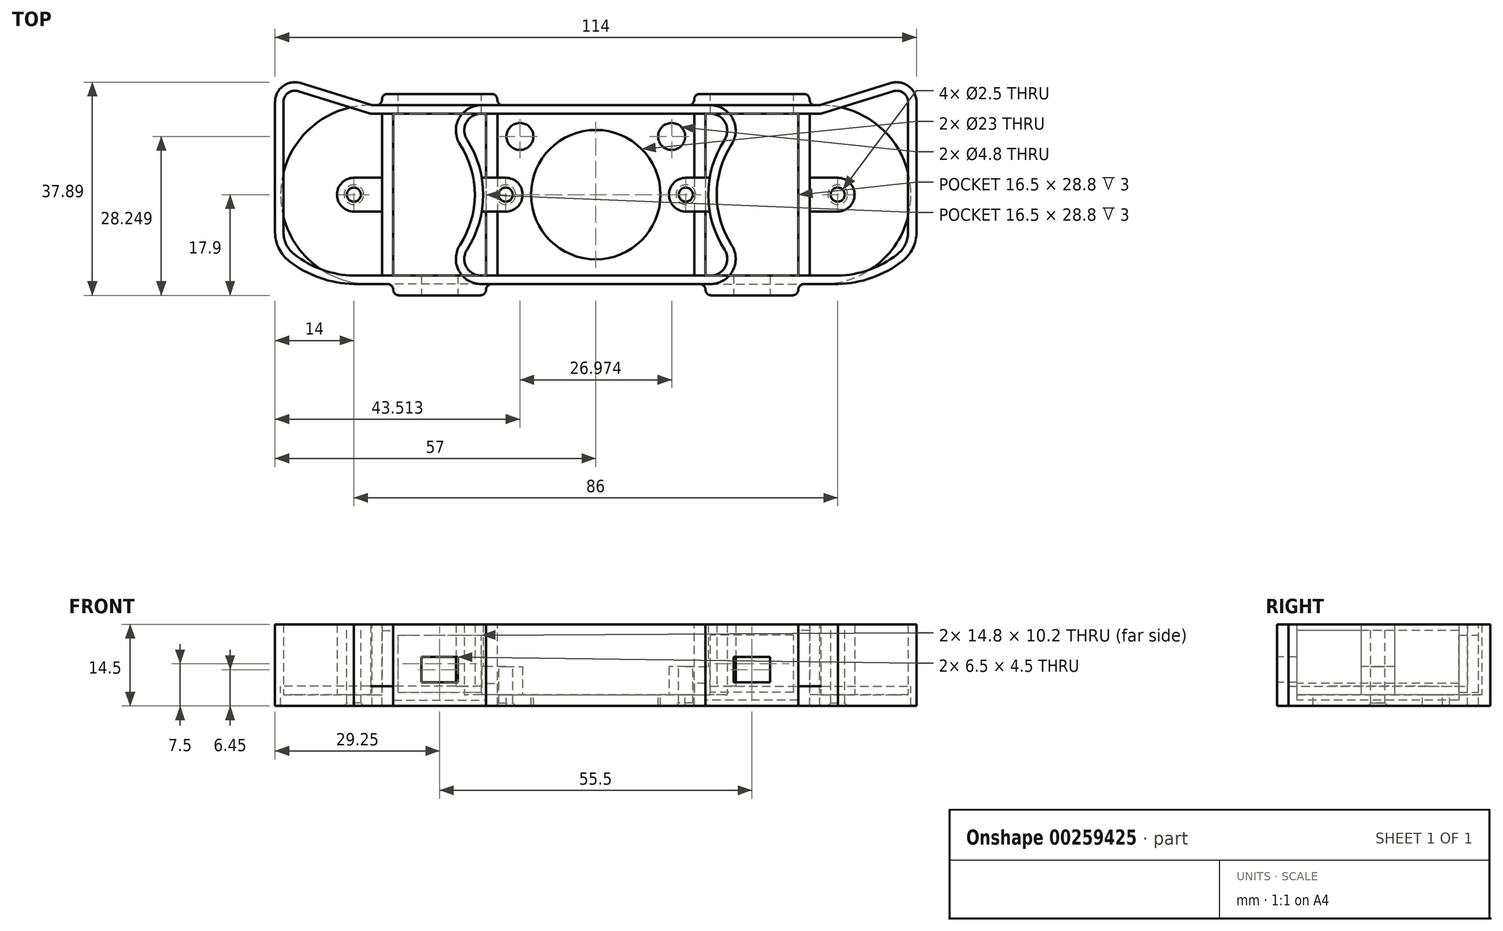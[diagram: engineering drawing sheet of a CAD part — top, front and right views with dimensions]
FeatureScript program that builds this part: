
annotation { "Feature Type Name" : "Feature", "Feature Type Description" : "" }
export const myFeature = defineFeature(function(context is Context, id is Id, definition is map)
    precondition{}
    {
        {
            var Q0;
            Q0=qCreatedBy(makeId("Top.planeOp"),FACE);
            var sketch = newSketch(context, id + "F0", { "sketchPlane" : qUnion([Q0])});
            skCircle(sketch, "E0", {"center": v(16, 0) * mm, "radius": 1.25 * mm});
            skCircle(sketch, "E1", {"center": v(-43, 0) * mm, "radius": 1.25 * mm});
            skCircle(sketch, "E2", {"center": v(0, 0) * mm, "radius": 11.5 * mm});
            skLineSegment(sketch, "E3", {"start": v(-40, 14.4) * mm, "end": v(20, 14.4) * mm});
            skLineSegment(sketch, "E4", {"start": v(-43, -14.4) * mm, "end": v(20, -14.4) * mm});
            skCircle(sketch, "E5", {"center": v(13.49, 10.35) * mm, "radius": 2.4 * mm});
            skLineSegment(sketch, "E6", {"start": v(-55.5, 14.4) * mm, "end": v(-55.5, -6.69) * mm});
            skLineSegment(sketch, "E7", {"start": v(20, 14.4) * mm, "end": v(20, -14.4) * mm, "construction": true});
            skArc(sketch, "E8", {"start": v(22.88, 9.77) * mm, "mid": v(20, 0) * mm, "end": v(22.88, -9.77) * mm});
            skLineSegment(sketch, "E9", {"start": v(20, 14.4) * mm, "end": v(20.36, 14.4) * mm});
            skLineSegment(sketch, "E10", {"start": v(20, -14.4) * mm, "end": v(20.36, -14.4) * mm});
            skPoint(sketch, "E11.visualSharp", {"position": v(27.2, 14.4) * mm});
            skArc(sketch, "E11.filletArc", {"start": v(22.88, 9.77) * mm, "mid": v(23, 12.83) * mm, "end": v(20.36, 14.4) * mm});
            skPoint(sketch, "E12.visualSharp", {"position": v(27.2, -14.4) * mm});
            skArc(sketch, "E12.filletArc", {"start": v(20.36, -14.4) * mm, "mid": v(23, -12.83) * mm, "end": v(22.88, -9.77) * mm});
            skLineSegment(sketch, "E13", {"start": v(-40, 14.4) * mm, "end": v(-52.9, 18.4) * mm});
            skLineSegment(sketch, "E14", {"start": v(-55.5, 16.49) * mm, "end": v(-55.5, 14.4) * mm});
            skLineSegment(sketch, "E15", {"start": v(-55.5, 14.4) * mm, "end": v(-40, 14.4) * mm, "construction": true});
            skArc(sketch, "E16", {"start": v(-53.56, -10.64) * mm, "mid": v(-48.58, -13.36) * mm, "end": v(-43, -14.4) * mm});
            skPoint(sketch, "E17.orphan", {"position": v(-55.5, -14.4) * mm});
            skPoint(sketch, "E18.visualSharp", {"position": v(-55.5, 19.2) * mm});
            skArc(sketch, "E18.filletArc", {"start": v(-52.9, 18.4) * mm, "mid": v(-54.69, 18.1) * mm, "end": v(-55.5, 16.49) * mm});
            skPoint(sketch, "E19.visualSharp", {"position": v(-55.5, -8.9) * mm});
            skArc(sketch, "E19.filletArc", {"start": v(-55.5, -6.69) * mm, "mid": v(-54.99, -8.89) * mm, "end": v(-53.56, -10.64) * mm});
            skLineSegment(sketch, "E20.0", {"start": v(-39.77, 15.9) * mm, "end": v(-52.46, 19.83) * mm});
            skArc(sketch, "E20.1", {"start": v(-52.46, 19.83) * mm, "mid": v(-55.58, 19.3) * mm, "end": v(-57, 16.49) * mm});
            skArc(sketch, "E20.2", {"start": v(20.36, -15.9) * mm, "mid": v(24.32, -13.55) * mm, "end": v(24.14, -8.96) * mm});
            skArc(sketch, "E20.3", {"start": v(24.14, 8.96) * mm, "mid": v(21.5, 0) * mm, "end": v(24.14, -8.96) * mm});
            skArc(sketch, "E20.4", {"start": v(24.14, 8.96) * mm, "mid": v(24.32, 13.55) * mm, "end": v(20.36, 15.9) * mm});
            skLineSegment(sketch, "E20.5", {"start": v(20, 15.9) * mm, "end": v(20.36, 15.9) * mm});
            skLineSegment(sketch, "E20.6", {"start": v(20, -15.9) * mm, "end": v(20.36, -15.9) * mm});
            skLineSegment(sketch, "E20.7", {"start": v(-43.02, -15.9) * mm, "end": v(20, -15.9) * mm});
            skLineSegment(sketch, "E20.8", {"start": v(-39.77, 15.9) * mm, "end": v(20, 15.9) * mm});
            skArc(sketch, "E20.9", {"start": v(-54.48, -11.83) * mm, "mid": v(-49.07, -14.78) * mm, "end": v(-43.02, -15.9) * mm});
            skArc(sketch, "E20.10", {"start": v(-57, -6.69) * mm, "mid": v(-56.34, -9.55) * mm, "end": v(-54.48, -11.83) * mm});
            skLineSegment(sketch, "E20.11", {"start": v(-57, 14.4) * mm, "end": v(-57, -6.69) * mm});
            skLineSegment(sketch, "E20.12", {"start": v(-57, 16.49) * mm, "end": v(-57, 14.4) * mm});
            skCircle(sketch, "E21", {"center": v(40.1, 0) * mm, "radius": 15.9 * mm});
            skLineSegment(sketch, "E22", {"start": v(20.36, 15.9) * mm, "end": v(40.1, 15.9) * mm});
            skLineSegment(sketch, "E23", {"start": v(20.36, -15.9) * mm, "end": v(40.1, -15.9) * mm});
            skLineSegment(sketch, "E24", {"start": v(-36, 14.4) * mm, "end": v(-36, -14.4) * mm});
            skLineSegment(sketch, "E25", {"start": v(-19.5, 14.4) * mm, "end": v(-19.5, -14.4) * mm});
            skLineSegment(sketch, "E26", {"start": v(-17.5, 14.4) * mm, "end": v(-17.5, -14.4) * mm});
            skLineSegment(sketch, "E27", {"start": v(-38, 14.4) * mm, "end": v(-38, -14.4) * mm});
            skArc(sketch, "E28", {"start": v(-43, 3) * mm, "mid": v(-46, 0) * mm, "end": v(-43, -3) * mm});
            skLineSegment(sketch, "E29", {"start": v(-43, -3) * mm, "end": v(-38, -3) * mm});
            skLineSegment(sketch, "E30", {"start": v(-43, 3) * mm, "end": v(-38, 3) * mm});
            skArc(sketch, "E31", {"start": v(16, 3) * mm, "mid": v(13, 0) * mm, "end": v(16, -3) * mm});
            skLineSegment(sketch, "E32", {"start": v(16, 3) * mm, "end": v(20.25, 3) * mm});
            skLineSegment(sketch, "E33", {"start": v(16, -3) * mm, "end": v(20.25, -3) * mm});
            skLineSegment(sketch, "E34", {"start": v(-38, 15.9) * mm, "end": v(-38, 17.9) * mm});
            skLineSegment(sketch, "E35", {"start": v(-38, 17.9) * mm, "end": v(-17.5, 17.9) * mm});
            skLineSegment(sketch, "E36", {"start": v(-17.5, 17.9) * mm, "end": v(-17.5, 15.9) * mm});
            skLineSegment(sketch, "E37", {"start": v(-36, -15.9) * mm, "end": v(-36, -17.9) * mm});
            skLineSegment(sketch, "E38", {"start": v(-36, -17.9) * mm, "end": v(-19.5, -17.9) * mm});
            skLineSegment(sketch, "E39", {"start": v(-19.5, -17.9) * mm, "end": v(-19.5, -15.9) * mm});
            skLineSegment(sketch, "E40", {"start": v(-35, 17.9) * mm, "end": v(-35, 14.4) * mm});
            skLineSegment(sketch, "E41", {"start": v(-20.5, 17.9) * mm, "end": v(-20.5, 14.4) * mm});
            skLineSegment(sketch, "E42", {"start": v(-31, -14.4) * mm, "end": v(-31, -17.9) * mm});
            skLineSegment(sketch, "E43", {"start": v(-24.5, -14.4) * mm, "end": v(-24.5, -17.9) * mm});
            skSolve(sketch);
        }
        {
            var Q0;
            Q0 = qSketchRegion(id + "F0", true);
            var Q1;
            Q1=makeQuery(id+"F0.imprint","IMPRINT",FACE,{"disambiguationData":[TD([[makeQuery(id+"F0.imprint","IMPRINT",EDGE,{"derivedFrom":sQuery(id+"F0.wireOp",EDGE,"E2")}),-1.0]])]});
            var Q2;
            {var subQ0=sQuery(id+"F0.wireOp",EDGE,"E40");var subQ1=sQuery(id+"F0.wireOp",EDGE,"E3");var subQ2=makeQuery(id+"F0.imprint","INTERSECT",VERTEX,{"derivedFrom":[subQ1,subQ0]});Q2=makeQuery(id+"F0.imprint","IMPRINT",FACE,{"disambiguationData":[TD([[makeQuery(id+"F0.imprint","IMPRINT",EDGE,{"disambiguationData":[TD([[subQ2,-1.0]])],"derivedFrom":subQ1}),1.0]])]});}
            var Q3;
            {var subQ0=sQuery(id+"F0.wireOp",EDGE,"E24");Q3=makeQuery(id+"F0.imprint","IMPRINT",FACE,{"disambiguationData":[TD([[makeQuery(id+"F0.imprint","IMPRINT",EDGE,{"derivedFrom":subQ0}),1.0]])]});}
            var Q4;
            {var subQ4=sQuery(id+"F0.wireOp",EDGE,"E24");Q4=makeQuery(id+"F0.imprint","IMPRINT",FACE,{"disambiguationData":[TD([[makeQuery(id+"F0.imprint","IMPRINT",EDGE,{"derivedFrom":subQ4}),-1.0]])]});}
            var Q5;
            Q5=makeQuery(id+"F0.imprint","IMPRINT",FACE,{"disambiguationData":[TD([[makeQuery(id+"F0.imprint","IMPRINT",EDGE,{"derivedFrom":sQuery(id+"F0.wireOp",EDGE,"E1")}),-1.0]])]});
            var Q6;
            Q6=makeQuery(id+"F0.imprint","IMPRINT",FACE,{"disambiguationData":[TD([[makeQuery(id+"F0.imprint","IMPRINT",EDGE,{"derivedFrom":sQuery(id+"F0.wireOp",EDGE,"E6")}),1.0]])]});
            var Q7;
            {var subQ0=sQuery(id+"F0.wireOp",EDGE,"E25");Q7=makeQuery(id+"F0.imprint","IMPRINT",FACE,{"disambiguationData":[TD([[makeQuery(id+"F0.imprint","IMPRINT",EDGE,{"derivedFrom":subQ0}),1.0]])]});}
            var Q8;
            Q8=makeQuery(id+"F0.imprint","IMPRINT",FACE,{"disambiguationData":[TD([[makeQuery(id+"F0.imprint","IMPRINT",EDGE,{"derivedFrom":sQuery(id+"F0.wireOp",EDGE,"E0")}),-1.0]])]});
            var Q9;
            {var subQ0=sQuery(id+"F0.wireOp",EDGE,"E42");var subQ1=sQuery(id+"F0.wireOp",EDGE,"E4");var subQ2=makeQuery(id+"F0.imprint","INTERSECT",VERTEX,{"derivedFrom":[subQ1,subQ0]});Q9=makeQuery(id+"F0.imprint","IMPRINT",FACE,{"disambiguationData":[TD([[makeQuery(id+"F0.imprint","IMPRINT",EDGE,{"disambiguationData":[TD([[subQ2,-1.0]])],"derivedFrom":subQ1}),-1.0]])]});}
            extrude(context, id + "F1", {"entities" : qUnion([Q0, Q1, Q2, Q3, Q4, Q5, Q6, Q7, Q8, Q9]), "oppositeDirection" : true, "depth" : 2 * mm});
        }
        {
            var Q0;
            Q0=makeQuery(id+"F0.imprint","IMPRINT",FACE,{"disambiguationData":[TD([[makeQuery(id+"F0.imprint","IMPRINT",EDGE,{"derivedFrom":sQuery(id+"F0.wireOp",EDGE,"E20.2")}),-1.0]])]});
            var Q1;
            {var subQ0=sQuery(id+"F0.wireOp",EDGE,"E21");var subQ1=makeQuery(id+"F0.imprint","INTERSECT",VERTEX,{"derivedFrom":[subQ0,sQuery(id+"F0.wireOp",EDGE,"E22")]});Q1=makeQuery(id+"F0.imprint","IMPRINT",FACE,{"disambiguationData":[TD([[makeQuery(id+"F0.imprint","IMPRINT",EDGE,{"disambiguationData":[TD([[subQ1,-1.0]])],"derivedFrom":subQ0}),1.0]])]});}
            extrude(context, id + "F2", {"entities" : qUnion([Q0, Q1]), "operationType" : NewBodyOperationType.ADD, "depth" : 1.5 * mm});
        }
        {
            var Q0;
            {var subQ4=sQuery(id+"F0.wireOp",EDGE,"E24");Q0=makeQuery(id+"F0.imprint","IMPRINT",FACE,{"disambiguationData":[TD([[makeQuery(id+"F0.imprint","IMPRINT",EDGE,{"derivedFrom":subQ4}),-1.0]])]});}
            extrude(context, id + "F3", {"entities" : qUnion([Q0]), "operationType" : NewBodyOperationType.ADD, "depth" : 11.4 * mm});
        }
        {
            var Q0;
            {var subQ0=sQuery(id+"F0.wireOp",EDGE,"E25");Q0=makeQuery(id+"F0.imprint","IMPRINT",FACE,{"disambiguationData":[TD([[makeQuery(id+"F0.imprint","IMPRINT",EDGE,{"derivedFrom":subQ0}),1.0]])]});}
            extrude(context, id + "F4", {"entities" : qUnion([Q0]), "operationType" : NewBodyOperationType.ADD, "depth" : 2 * mm});
        }
        {
            var Q0;
            {var subQ22=sQuery(id+"F0.wireOp",EDGE,"E9");Q0=makeQuery(id+"F0.imprint","IMPRINT",FACE,{"disambiguationData":[TD([[makeQuery(id+"F0.imprint","IMPRINT",EDGE,{"derivedFrom":subQ22}),1.0]])]});}
            var Q1;
            Q1=makeQuery(id+"F0.imprint","IMPRINT",FACE,{"disambiguationData":[TD([[makeQuery(id+"F0.imprint","IMPRINT",EDGE,{"derivedFrom":sQuery(id+"F0.wireOp",EDGE,"E6")}),-1.0]])]});
            var Q2;
            {var subQ0=sQuery(id+"F0.wireOp",EDGE,"E37");Q2=makeQuery(id+"F0.imprint","IMPRINT",FACE,{"disambiguationData":[TD([[makeQuery(id+"F0.imprint","IMPRINT",EDGE,{"derivedFrom":subQ0}),1.0]])]});}
            var Q3;
            {var subQ0=sQuery(id+"F0.wireOp",EDGE,"E39");Q3=makeQuery(id+"F0.imprint","IMPRINT",FACE,{"disambiguationData":[TD([[makeQuery(id+"F0.imprint","IMPRINT",EDGE,{"derivedFrom":subQ0}),1.0]])]});}
            var Q4;
            {var subQ0=sQuery(id+"F0.wireOp",EDGE,"E42");var subQ1=sQuery(id+"F0.wireOp",EDGE,"E20.7");var subQ2=makeQuery(id+"F0.imprint","INTERSECT",VERTEX,{"derivedFrom":[subQ1,subQ0]});Q4=makeQuery(id+"F0.imprint","IMPRINT",FACE,{"disambiguationData":[TD([[makeQuery(id+"F0.imprint","IMPRINT",EDGE,{"disambiguationData":[TD([[subQ2,-1.0]])],"derivedFrom":subQ1}),-1.0]])]});}
            var Q5;
            {var subQ0=sQuery(id+"F0.wireOp",EDGE,"E42");var subQ1=sQuery(id+"F0.wireOp",EDGE,"E4");var subQ2=makeQuery(id+"F0.imprint","INTERSECT",VERTEX,{"derivedFrom":[subQ1,subQ0]});Q5=makeQuery(id+"F0.imprint","IMPRINT",FACE,{"disambiguationData":[TD([[makeQuery(id+"F0.imprint","IMPRINT",EDGE,{"disambiguationData":[TD([[subQ2,-1.0]])],"derivedFrom":subQ1}),-1.0]])]});}
            var Q6;
            {var subQ0=sQuery(id+"F0.wireOp",EDGE,"E34");Q6=makeQuery(id+"F0.imprint","IMPRINT",FACE,{"disambiguationData":[TD([[makeQuery(id+"F0.imprint","IMPRINT",EDGE,{"derivedFrom":subQ0}),-1.0]])]});}
            var Q7;
            {var subQ0=sQuery(id+"F0.wireOp",EDGE,"E40");var subQ1=sQuery(id+"F0.wireOp",EDGE,"E3");var subQ2=makeQuery(id+"F0.imprint","INTERSECT",VERTEX,{"derivedFrom":[subQ1,subQ0]});Q7=makeQuery(id+"F0.imprint","IMPRINT",FACE,{"disambiguationData":[TD([[makeQuery(id+"F0.imprint","IMPRINT",EDGE,{"disambiguationData":[TD([[subQ2,-1.0]])],"derivedFrom":subQ1}),1.0]])]});}
            var Q8;
            {var subQ0=sQuery(id+"F0.wireOp",EDGE,"E40");var subQ1=sQuery(id+"F0.wireOp",EDGE,"E20.8");var subQ2=makeQuery(id+"F0.imprint","INTERSECT",VERTEX,{"derivedFrom":[subQ1,subQ0]});Q8=makeQuery(id+"F0.imprint","IMPRINT",FACE,{"disambiguationData":[TD([[makeQuery(id+"F0.imprint","IMPRINT",EDGE,{"disambiguationData":[TD([[subQ2,-1.0]])],"derivedFrom":subQ1}),1.0]])]});}
            var Q9;
            {var subQ0=sQuery(id+"F0.wireOp",EDGE,"E36");Q9=makeQuery(id+"F0.imprint","IMPRINT",FACE,{"disambiguationData":[TD([[makeQuery(id+"F0.imprint","IMPRINT",EDGE,{"derivedFrom":subQ0}),-1.0]])]});}
            var Q10;
            Q10=makeQuery(id+"F0.imprint","IMPRINT",FACE,{"disambiguationData":[TD([[makeQuery(id+"F0.imprint","IMPRINT",EDGE,{"derivedFrom":sQuery(id+"F0.wireOp",EDGE,"E1")}),-1.0]])]});
            extrude(context, id + "F5", {"entities" : qUnion([Q0, Q1, Q2, Q3, Q4, Q5, Q6, Q7, Q8, Q9, Q10]), "operationType" : NewBodyOperationType.ADD, "depth" : 12.5 * mm});
        }
        {
            var Q0;
            {var subQ0=sQuery(id+"F0.wireOp",EDGE,"E24");Q0=makeQuery(id+"F0.imprint","IMPRINT",FACE,{"disambiguationData":[TD([[makeQuery(id+"F0.imprint","IMPRINT",EDGE,{"derivedFrom":subQ0}),1.0]])]});}
            extrude(context, id + "F6", {"entities" : qUnion([Q0]), "operationType" : NewBodyOperationType.REMOVE, "oppositeDirection" : true, "depth" : 1 * mm});
        }
        {
            var Q0;
            {var subQ0=sQuery(id+"F0.wireOp",EDGE,"E38");Q0=makeQuery(id+"F5.boolean.opBoolean","MERGE",FACE,{"derivedFrom":[makeQuery(id+"F1.opExtrude","SWEPT_FACE",FACE,{"disambiguationData":[OSD([subQ0])]}),makeQuery(id+"F5.opExtrude","SWEPT_FACE",FACE,{"disambiguationData":[OSD([subQ0])]})]});}
            var sketch = newSketch(context, id + "F7", { "sketchPlane" : qUnion([Q0])});
            skLineSegment(sketch, "E44", {"start": v(-36, -2) * mm, "end": v(-19.5, 12.5) * mm, "construction": true});
            skLineSegment(sketch, "E45", {"start": v(-19.5, 12.5) * mm, "end": v(-36, 12.5) * mm, "construction": true});
            skLineSegment(sketch, "E46", {"start": v(-36, 12.5) * mm, "end": v(-19.5, -2) * mm, "construction": true});
            skLineSegment(sketch, "E47", {"start": v(-27.75, 5.25) * mm, "end": v(-27.75, -2) * mm, "construction": true});
            skLineSegment(sketch, "E48.bottom", {"start": v(-24.5, 2.2) * mm, "end": v(-31, 2.2) * mm});
            skLineSegment(sketch, "E48.top", {"start": v(-24.5, 6.7) * mm, "end": v(-31, 6.7) * mm});
            skLineSegment(sketch, "E48.left", {"start": v(-24.5, 2.2) * mm, "end": v(-24.5, 6.7) * mm});
            skLineSegment(sketch, "E48.right", {"start": v(-31, 2.2) * mm, "end": v(-31, 6.7) * mm});
            skPoint(sketch, "E48.middle", {"position": v(-27.75, 4.45) * mm});
            skSolve(sketch);
        }
        {
            var Q0;
            Q0 = qSketchRegion(id + "F7", true);
            extrude(context, id + "F8", {"entities" : qUnion([Q0]), "operationType" : NewBodyOperationType.REMOVE, "oppositeDirection" : true, "depth" : 25 * mm});
        }
        {
            var Q0;
            {var subQ0=sQuery(id+"F0.wireOp",EDGE,"E35");Q0=makeQuery(id+"F5.boolean.opBoolean","MERGE",FACE,{"derivedFrom":[makeQuery(id+"F1.opExtrude","SWEPT_FACE",FACE,{"disambiguationData":[OSD([subQ0])]}),makeQuery(id+"F5.opExtrude","SWEPT_FACE",FACE,{"disambiguationData":[OSD([subQ0])]})]});}
            var sketch = newSketch(context, id + "F9", { "sketchPlane" : qUnion([Q0])});
            skLineSegment(sketch, "E49", {"start": v(17.5, 12.5) * mm, "end": v(38, -2) * mm, "construction": true});
            skLineSegment(sketch, "E50", {"start": v(38, -2) * mm, "end": v(38, 12.5) * mm, "construction": true});
            skLineSegment(sketch, "E51", {"start": v(38, 12.5) * mm, "end": v(17.5, -2) * mm, "construction": true});
            skLineSegment(sketch, "E52", {"start": v(27.75, 8.75) * mm, "end": v(27.75, 1.22) * mm, "construction": true});
            skPoint(sketch, "E52.startSnap0", {"position": v(27.75, 5.25) * mm});
            skLineSegment(sketch, "E53.bottom", {"start": v(35.15, 0.4) * mm, "end": v(20.35, 0.4) * mm});
            skLineSegment(sketch, "E53.top", {"start": v(35.15, 10.6) * mm, "end": v(20.35, 10.6) * mm});
            skLineSegment(sketch, "E53.left", {"start": v(35.15, 0.4) * mm, "end": v(35.15, 10.6) * mm});
            skLineSegment(sketch, "E53.right", {"start": v(20.35, 0.4) * mm, "end": v(20.35, 10.6) * mm});
            skPoint(sketch, "E53.middle", {"position": v(27.75, 5.5) * mm});
            skSolve(sketch);
        }
        {
            var Q0;
            Q0=makeQuery(id+"F9.imprint","IMPRINT",FACE,{"disambiguationData":[TD([[makeQuery(id+"F9.imprint","IMPRINT",EDGE,{"derivedFrom":sQuery(id+"F9.wireOp",EDGE,"E53.bottom")}),-1.0]])]});
            extrude(context, id + "F10", {"entities" : qUnion([Q0]), "operationType" : NewBodyOperationType.REMOVE, "oppositeDirection" : true, "depth" : 25 * mm});
        }
        {
            var Q0;
            {var subQ0=sQuery(id+"F0.wireOp",EDGE,"E36");var subQ1=sQuery(id+"F0.wireOp",EDGE,"E35");Q0=makeQuery(id+"F5.boolean.opBoolean","MERGE",EDGE,{"derivedFrom":[makeQuery(id+"F1.opExtrude","SWEPT_EDGE",EDGE,{"disambiguationData":[OSD([subQ1,subQ0])]}),makeQuery(id+"F5.opExtrude","SWEPT_EDGE",EDGE,{"disambiguationData":[OSD([subQ1,subQ0])]})]});}
            var Q1;
            {var subQ0=sQuery(id+"F0.wireOp",EDGE,"E35");var subQ1=sQuery(id+"F0.wireOp",EDGE,"E34");Q1=makeQuery(id+"F5.boolean.opBoolean","MERGE",EDGE,{"derivedFrom":[makeQuery(id+"F1.opExtrude","SWEPT_EDGE",EDGE,{"disambiguationData":[OSD([subQ1,subQ0])]}),makeQuery(id+"F5.opExtrude","SWEPT_EDGE",EDGE,{"disambiguationData":[OSD([subQ1,subQ0])]})]});}
            var Q2;
            {var subQ0=sQuery(id+"F0.wireOp",EDGE,"E36");var subQ1=sQuery(id+"F0.wireOp",EDGE,"E20.8");Q2=makeQuery(id+"F5.boolean.opBoolean","MERGE",EDGE,{"derivedFrom":[makeQuery(id+"F1.opExtrude","SWEPT_EDGE",EDGE,{"disambiguationData":[OSD([subQ1,subQ0])]}),makeQuery(id+"F5.opExtrude","SWEPT_EDGE",EDGE,{"disambiguationData":[OSD([subQ1,subQ0])]})]});}
            var Q3;
            {var subQ0=sQuery(id+"F0.wireOp",EDGE,"E34");var subQ1=sQuery(id+"F0.wireOp",EDGE,"E20.8");Q3=makeQuery(id+"F5.boolean.opBoolean","MERGE",EDGE,{"derivedFrom":[makeQuery(id+"F1.opExtrude","SWEPT_EDGE",EDGE,{"disambiguationData":[OSD([subQ1,subQ0])]}),makeQuery(id+"F5.opExtrude","SWEPT_EDGE",EDGE,{"disambiguationData":[OSD([subQ1,subQ0])]})]});}
            var Q4;
            {var subQ0=sQuery(id+"F0.wireOp",EDGE,"E39");var subQ1=sQuery(id+"F0.wireOp",EDGE,"E38");Q4=makeQuery(id+"F5.boolean.opBoolean","MERGE",EDGE,{"derivedFrom":[makeQuery(id+"F1.opExtrude","SWEPT_EDGE",EDGE,{"disambiguationData":[OSD([subQ1,subQ0])]}),makeQuery(id+"F5.opExtrude","SWEPT_EDGE",EDGE,{"disambiguationData":[OSD([subQ1,subQ0])]})]});}
            var Q5;
            {var subQ0=sQuery(id+"F0.wireOp",EDGE,"E39");var subQ1=sQuery(id+"F0.wireOp",EDGE,"E20.7");Q5=makeQuery(id+"F5.boolean.opBoolean","MERGE",EDGE,{"derivedFrom":[makeQuery(id+"F1.opExtrude","SWEPT_EDGE",EDGE,{"disambiguationData":[OSD([subQ1,subQ0])]}),makeQuery(id+"F5.opExtrude","SWEPT_EDGE",EDGE,{"disambiguationData":[OSD([subQ1,subQ0])]})]});}
            var Q6;
            {var subQ0=sQuery(id+"F0.wireOp",EDGE,"E37");var subQ1=sQuery(id+"F0.wireOp",EDGE,"E20.7");Q6=makeQuery(id+"F5.boolean.opBoolean","MERGE",EDGE,{"derivedFrom":[makeQuery(id+"F1.opExtrude","SWEPT_EDGE",EDGE,{"disambiguationData":[OSD([subQ1,subQ0])]}),makeQuery(id+"F5.opExtrude","SWEPT_EDGE",EDGE,{"disambiguationData":[OSD([subQ1,subQ0])]})]});}
            var Q7;
            {var subQ0=sQuery(id+"F0.wireOp",EDGE,"E38");var subQ1=sQuery(id+"F0.wireOp",EDGE,"E37");Q7=makeQuery(id+"F5.boolean.opBoolean","MERGE",EDGE,{"derivedFrom":[makeQuery(id+"F1.opExtrude","SWEPT_EDGE",EDGE,{"disambiguationData":[OSD([subQ1,subQ0])]}),makeQuery(id+"F5.opExtrude","SWEPT_EDGE",EDGE,{"disambiguationData":[OSD([subQ1,subQ0])]})]});}
            fillet(context, id + "F11", {"entities" : qUnion([Q0, Q1, Q2, Q3, Q4, Q5, Q6, Q7]), "radius" : 1 * mm, "tangentPropagation" : true, "allowEdgeOverflow" : false});
        }
        {
            var Q0;
            Q0=makeQuery(id+"F0.imprint","IMPRINT",FACE,{"disambiguationData":[TD([[makeQuery(id+"F0.imprint","IMPRINT",EDGE,{"derivedFrom":sQuery(id+"F0.wireOp",EDGE,"E0")}),-1.0]])]});
            extrude(context, id + "F12", {"entities" : qUnion([Q0]), "operationType" : NewBodyOperationType.ADD, "depth" : 5 * mm});
        }
        {
            var Q0;
            Q0=makeQuery(id+"F1.opExtrude","CAP_EDGE",EDGE,{"disambiguationData":[OSD([sQuery(id+"F0.wireOp",EDGE,"E1")])],"isStart":false});
            var Q1;
            Q1=makeQuery(id+"F1.opExtrude","CAP_EDGE",EDGE,{"disambiguationData":[OSD([sQuery(id+"F0.wireOp",EDGE,"E0")])],"isStart":false});
            chamfer(context, id + "F13", {"entities" : qUnion([Q0, Q1]), "width" : 0.5 * mm, "tangentPropagation" : true});
        }
        {
            var Q0;
            Q0=makeQuery(id+"F1.opExtrude","SWEPT_BODY",BODY,{"disambiguationData":[OSD([sQuery(id+"F0.wireOp",EDGE,"E0"),sQuery(id+"F0.wireOp",EDGE,"E1"),sQuery(id+"F0.wireOp",EDGE,"E2"),sQuery(id+"F0.wireOp",EDGE,"E5"),sQuery(id+"F0.wireOp",EDGE,"E20.0"),sQuery(id+"F0.wireOp",EDGE,"E20.1"),sQuery(id+"F0.wireOp",EDGE,"E20.5"),sQuery(id+"F0.wireOp",EDGE,"E20.6"),sQuery(id+"F0.wireOp",EDGE,"E20.7"),sQuery(id+"F0.wireOp",EDGE,"E20.8"),sQuery(id+"F0.wireOp",EDGE,"E20.9"),sQuery(id+"F0.wireOp",EDGE,"E20.10"),sQuery(id+"F0.wireOp",EDGE,"E20.11"),sQuery(id+"F0.wireOp",EDGE,"E20.12"),sQuery(id+"F0.wireOp",EDGE,"E21"),sQuery(id+"F0.wireOp",EDGE,"E22"),sQuery(id+"F0.wireOp",EDGE,"E23"),sQuery(id+"F0.wireOp",EDGE,"E34"),sQuery(id+"F0.wireOp",EDGE,"E35"),sQuery(id+"F0.wireOp",EDGE,"E36"),sQuery(id+"F0.wireOp",EDGE,"E37"),sQuery(id+"F0.wireOp",EDGE,"E38"),sQuery(id+"F0.wireOp",EDGE,"E39")])]});
            var Q1;
            Q1=qCreatedBy(makeId("Right.planeOp"),FACE);
            mirror(context, id + "F14", {"entities" : qUnion([Q0]), "mirrorPlane" : qUnion([Q1])});
        }
    });
